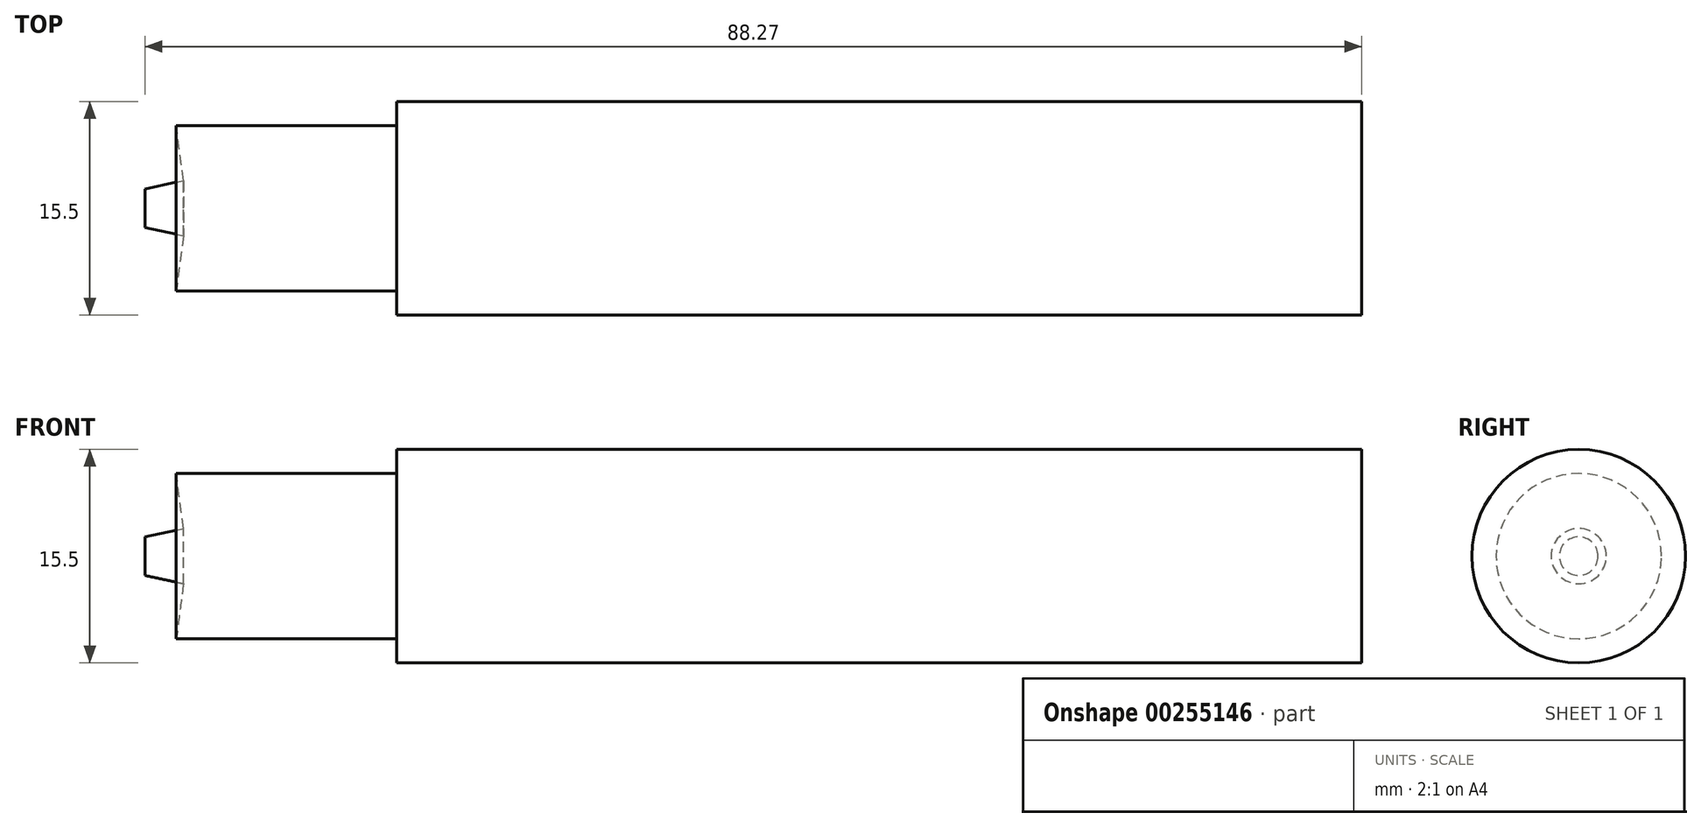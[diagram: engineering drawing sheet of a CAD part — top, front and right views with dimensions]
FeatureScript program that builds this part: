
annotation { "Feature Type Name" : "Feature", "Feature Type Description" : "" }
export const myFeature = defineFeature(function(context is Context, id is Id, definition is map)
    precondition{}
    {
        {
            var Q0;
            Q0=qCreatedBy(makeId("Front.planeOp"),FACE);
            var sketch = newSketch(context, id + "F0", { "sketchPlane" : qUnion([Q0])});
            skLineSegment(sketch, "E0", {"start": v(0, 0) * mm, "end": v(-88.27, 0) * mm});
            skLineSegment(sketch, "E1", {"start": v(0, 0) * mm, "end": v(0, 7.75) * mm});
            skLineSegment(sketch, "E2", {"start": v(-86, 6) * mm, "end": v(-85.47, 2) * mm});
            skLineSegment(sketch, "E3", {"start": v(-85.47, 2) * mm, "end": v(-88.27, 1.4) * mm});
            skLineSegment(sketch, "E4", {"start": v(-88.27, 1.4) * mm, "end": v(-88.27, 0) * mm});
            skLineSegment(sketch, "E5", {"start": v(-85.47, 2) * mm, "end": v(-85.47, 6) * mm, "construction": true});
            skLineSegment(sketch, "E6", {"start": v(-86, 6) * mm, "end": v(-70, 6) * mm});
            skLineSegment(sketch, "E7", {"start": v(-70, 6) * mm, "end": v(-70, 7.75) * mm});
            skLineSegment(sketch, "E8", {"start": v(-70, 7.75) * mm, "end": v(0, 7.75) * mm});
            skSolve(sketch);
        }
        {
            var Q0;
            Q0 = qSketchRegion(id + "F0", true);
            var Q1;
            Q1=sQuery(id+"F0.wireOp",EDGE,"E0");
            revolve(context, id + "F1", {"entities" : qUnion([Q0]), "axis" : qUnion([Q1]), "revolveType" : RevolveType.FULL});
        }
    });
